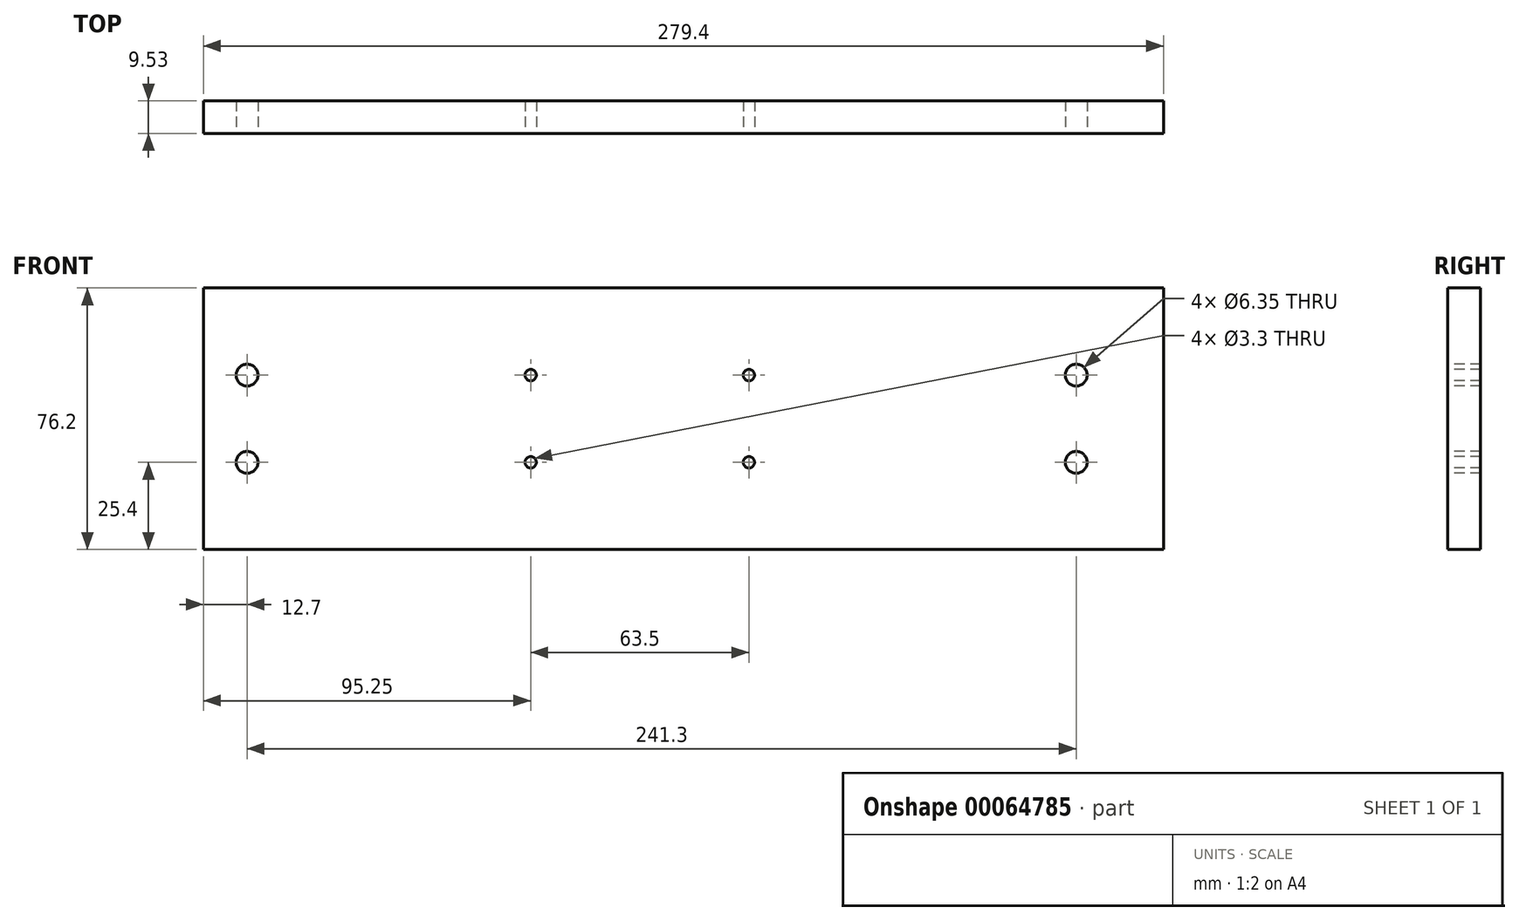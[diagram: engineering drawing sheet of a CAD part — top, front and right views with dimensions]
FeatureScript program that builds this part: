
annotation { "Feature Type Name" : "Feature", "Feature Type Description" : "" }
export const myFeature = defineFeature(function(context is Context, id is Id, definition is map)
    precondition{}
    {
        {
            var Q0;
            Q0=qCreatedBy(makeId("Front.planeOp"),FACE);
            var sketch = newSketch(context, id + "F0", { "sketchPlane" : qUnion([Q0])});
            skLineSegment(sketch, "E0.bottom", {"start": v(0, 0) * mm, "end": v(279.4, 0) * mm});
            skLineSegment(sketch, "E0.top", {"start": v(0, 76.2) * mm, "end": v(279.4, 76.2) * mm});
            skLineSegment(sketch, "E0.left", {"start": v(0, 0) * mm, "end": v(0, 76.2) * mm});
            skLineSegment(sketch, "E0.right", {"start": v(279.4, 0) * mm, "end": v(279.4, 76.2) * mm});
            skSolve(sketch);
        }
        {
            var Q0;
            Q0=qSketchRegion(id+"F0",true);
            extrude(context, id + "F1", {"entities" : qUnion([Q0]), "depth" : 9.52 * mm});
        }
        {
            var Q0;
            Q0=makeQuery(id+"F1.opExtrude","CAP_FACE",FACE,{"disambiguationData":[OSD([sQuery(id+"F0.wireOp",EDGE,"E0.bottom"),sQuery(id+"F0.wireOp",EDGE,"E0.top"),sQuery(id+"F0.wireOp",EDGE,"E0.left"),sQuery(id+"F0.wireOp",EDGE,"E0.right")])],"isStart":false});
            var sketch = newSketch(context, id + "F2", { "sketchPlane" : qUnion([Q0])});
            skLineSegment(sketch, "E1", {"start": v(-24.93, 38.1) * mm, "end": v(287.6, 38.1) * mm, "construction": true});
            skPoint(sketch, "E1.startSnap0", {"position": v(0, 38.1) * mm});
            skPoint(sketch, "E2.startSnap0", {"position": v(139.7, 76.2) * mm});
            skLineSegment(sketch, "E3", {"start": v(139.7, 98.91) * mm, "end": v(139.7, -22.94) * mm, "construction": true});
            skCircle(sketch, "E4", {"center": v(12.7, 50.8) * mm, "radius": 3.18 * mm});
            skCircle(sketch, "E5", {"center": v(12.7, 25.4) * mm, "radius": 3.18 * mm});
            skCircle(sketch, "E6", {"center": v(95.25, 50.8) * mm, "radius": 1.65 * mm});
            skCircle(sketch, "E7", {"center": v(95.25, 25.4) * mm, "radius": 1.65 * mm});
            skCircle(sketch, "E8", {"center": v(158.75, 50.8) * mm, "radius": 1.65 * mm});
            skCircle(sketch, "E9", {"center": v(158.75, 25.4) * mm, "radius": 1.65 * mm});
            skCircle(sketch, "E10", {"center": v(254, 50.8) * mm, "radius": 3.18 * mm});
            skCircle(sketch, "E11", {"center": v(254, 25.4) * mm, "radius": 3.18 * mm});
            skSolve(sketch);
        }
        {
            var Q0;
            Q0=qSketchRegion(id+"F2",true);
            extrude(context, id + "F3", {"entities" : qUnion([Q0]), "operationType" : NewBodyOperationType.REMOVE, "endBound" : BoundingType.THROUGH_ALL, "oppositeDirection" : true, "depth" : 25.4 * mm, "hasSecondDirection" : true, "secondDirectionOppositeDirection" : false, "secondDirectionDepth" : 25.4 * mm});
        }
    });
